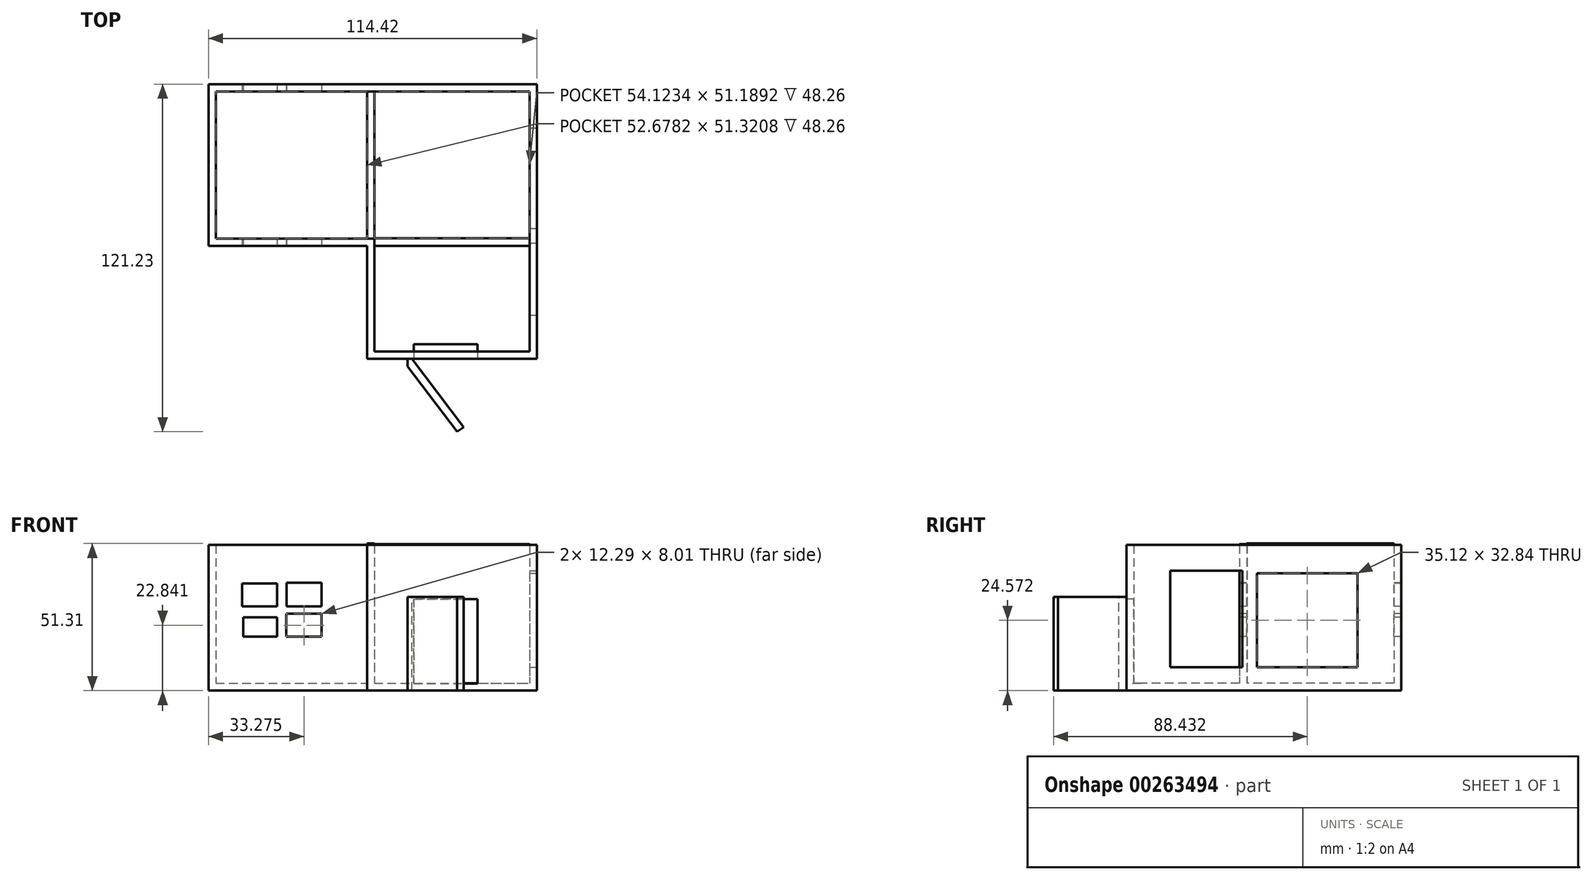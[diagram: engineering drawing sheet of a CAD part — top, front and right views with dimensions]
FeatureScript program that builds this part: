
annotation { "Feature Type Name" : "Feature", "Feature Type Description" : "" }
export const myFeature = defineFeature(function(context is Context, id is Id, definition is map)
    precondition{}
    {
        {
            var Q0;
            Q0=qCreatedBy(makeId("Top.planeOp"),FACE);
            var sketch = newSketch(context, id + "F0", { "sketchPlane" : qUnion([Q0])});
            skLineSegment(sketch, "E0.bottom", {"start": v(-55.22, 56.4) * mm, "end": v(59.2, 56.4) * mm});
            skLineSegment(sketch, "E0.top", {"start": v(-55.22, 0) * mm, "end": v(59.2, 0) * mm});
            skLineSegment(sketch, "E0.left", {"start": v(-55.22, 56.4) * mm, "end": v(-55.22, 0) * mm});
            skLineSegment(sketch, "E0.right", {"start": v(59.2, 56.4) * mm, "end": v(59.2, 0) * mm});
            skLineSegment(sketch, "E1.bottom", {"start": v(0, 0) * mm, "end": v(59.2, 0) * mm});
            skLineSegment(sketch, "E1.top", {"start": v(0, -39.43) * mm, "end": v(59.2, -39.43) * mm});
            skLineSegment(sketch, "E1.left", {"start": v(0, 0) * mm, "end": v(0, -39.43) * mm});
            skLineSegment(sketch, "E1.right", {"start": v(59.2, 0) * mm, "end": v(59.2, -39.43) * mm});
            skSolve(sketch);
        }
        {
            var Q0;
            Q0 = qSketchRegion(id + "F0", true);
            extrude(context, id + "F1", {"entities" : qUnion([Q0]), "depth" : 50.8 * mm});
        }
        {
            var Q0;
            Q0=makeQuery(id+"F1.opExtrude","CAP_FACE",FACE,{"disambiguationData":[OSD([sQuery(id+"F0.wireOp",EDGE,"E0.bottom"),sQuery(id+"F0.wireOp",EDGE,"E0.top"),sQuery(id+"F0.wireOp",EDGE,"E0.left"),sQuery(id+"F0.wireOp",EDGE,"E0.right"),sQuery(id+"F0.wireOp",EDGE,"E1.top"),sQuery(id+"F0.wireOp",EDGE,"E1.left"),sQuery(id+"F0.wireOp",EDGE,"E1.right")])],"isStart":false});
            shell(context, id + "F2", {"entities" : qUnion([Q0]), "thickness" : 2.54 * mm});
        }
        {
            var Q0;
            Q0=qCreatedBy(makeId("Front.planeOp"),FACE);
            var sketch = newSketch(context, id + "F3", { "sketchPlane" : qUnion([Q0])});
            skLineSegment(sketch, "E2.bottom", {"start": v(-43.44, 37.36) * mm, "end": v(-31.3, 37.36) * mm});
            skLineSegment(sketch, "E2.top", {"start": v(-43.44, 29.33) * mm, "end": v(-31.3, 29.33) * mm});
            skLineSegment(sketch, "E2.left", {"start": v(-43.44, 37.36) * mm, "end": v(-43.44, 29.33) * mm});
            skLineSegment(sketch, "E2.right", {"start": v(-31.3, 37.36) * mm, "end": v(-31.3, 29.33) * mm});
            skLineSegment(sketch, "E3.bottom", {"start": v(-27.97, 37.58) * mm, "end": v(-15.8, 37.58) * mm});
            skLineSegment(sketch, "E3.top", {"start": v(-27.97, 29.33) * mm, "end": v(-15.8, 29.33) * mm});
            skLineSegment(sketch, "E3.left", {"start": v(-27.97, 37.58) * mm, "end": v(-27.97, 29.33) * mm});
            skLineSegment(sketch, "E3.right", {"start": v(-15.8, 37.58) * mm, "end": v(-15.8, 29.33) * mm});
            skLineSegment(sketch, "E4.bottom", {"start": v(-28.1, 26.85) * mm, "end": v(-15.8, 26.85) * mm});
            skLineSegment(sketch, "E4.top", {"start": v(-28.1, 18.83) * mm, "end": v(-15.8, 18.83) * mm});
            skLineSegment(sketch, "E4.left", {"start": v(-28.1, 26.85) * mm, "end": v(-28.1, 18.83) * mm});
            skLineSegment(sketch, "E4.right", {"start": v(-15.8, 26.85) * mm, "end": v(-15.8, 18.83) * mm});
            skLineSegment(sketch, "E5.bottom", {"start": v(-31.3, 25.54) * mm, "end": v(-43.11, 25.54) * mm});
            skLineSegment(sketch, "E5.top", {"start": v(-31.3, 18.83) * mm, "end": v(-43.11, 18.83) * mm});
            skLineSegment(sketch, "E5.left", {"start": v(-31.3, 25.54) * mm, "end": v(-31.3, 18.83) * mm});
            skLineSegment(sketch, "E5.right", {"start": v(-43.11, 25.54) * mm, "end": v(-43.11, 18.83) * mm});
            skSolve(sketch);
        }
        {
            var Q0;
            Q0 = qSketchRegion(id + "F3", true);
            extrude(context, id + "F4", {"entities" : qUnion([Q0]), "operationType" : NewBodyOperationType.REMOVE, "oppositeDirection" : true, "depth" : 304.8 * mm});
        }
        {
            var Q0;
            Q0=makeQuery(id+"F1.opExtrude","SWEPT_FACE",FACE,{"disambiguationData":[OSD([sQuery(id+"F0.wireOp",EDGE,"E0.right"),sQuery(id+"F0.wireOp",EDGE,"E1.right")])]});
            var sketch = newSketch(context, id + "F5", { "sketchPlane" : qUnion([Q0])});
            skLineSegment(sketch, "E6.bottom", {"start": v(-24.19, 41.82) * mm, "end": v(0.96, 41.82) * mm});
            skLineSegment(sketch, "E6.top", {"start": v(-24.19, 8.15) * mm, "end": v(0.96, 8.15) * mm});
            skLineSegment(sketch, "E6.left", {"start": v(-24.19, 41.82) * mm, "end": v(-24.19, 8.15) * mm});
            skLineSegment(sketch, "E6.right", {"start": v(0.96, 41.82) * mm, "end": v(0.96, 8.15) * mm});
            skLineSegment(sketch, "E7.bottom", {"start": v(6.04, 41) * mm, "end": v(41.16, 41) * mm});
            skLineSegment(sketch, "E7.top", {"start": v(6.04, 8.15) * mm, "end": v(41.16, 8.15) * mm});
            skLineSegment(sketch, "E7.left", {"start": v(6.04, 41) * mm, "end": v(6.04, 8.15) * mm});
            skLineSegment(sketch, "E7.right", {"start": v(41.16, 41) * mm, "end": v(41.16, 8.15) * mm});
            skSolve(sketch);
        }
        {
            var Q0;
            Q0=makeQuery(id+"F5.imprint","IMPRINT",FACE,{"disambiguationData":[TD([[makeQuery(id+"F5.imprint","IMPRINT",EDGE,{"derivedFrom":sQuery(id+"F5.wireOp",EDGE,"E6.bottom")}),-1.0]])]});
            var Q1;
            Q1=makeQuery(id+"F5.imprint","IMPRINT",FACE,{"disambiguationData":[TD([[makeQuery(id+"F5.imprint","IMPRINT",EDGE,{"derivedFrom":sQuery(id+"F5.wireOp",EDGE,"E7.bottom")}),-1.0]])]});
            extrude(context, id + "F6", {"entities" : qUnion([Q0, Q1]), "operationType" : NewBodyOperationType.REMOVE, "oppositeDirection" : true, "depth" : 25.4 * mm});
        }
        {
            var Q0;
            Q0=makeQuery(id+"F1.opExtrude","SWEPT_FACE",FACE,{"disambiguationData":[OSD([sQuery(id+"F0.wireOp",EDGE,"E1.top")])]});
            var sketch = newSketch(context, id + "F7", { "sketchPlane" : qUnion([Q0])});
            skLineSegment(sketch, "E8.bottom", {"start": v(14.19, 0) * mm, "end": v(33.68, 0) * mm});
            skLineSegment(sketch, "E8.top", {"start": v(14.19, 32.67) * mm, "end": v(33.68, 32.67) * mm});
            skLineSegment(sketch, "E8.left", {"start": v(14.19, 0) * mm, "end": v(14.19, 32.67) * mm});
            skLineSegment(sketch, "E8.right", {"start": v(33.68, 0) * mm, "end": v(33.68, 32.67) * mm});
            skSolve(sketch);
        }
        {
            var Q0;
            Q0 = qSketchRegion(id + "F7", true);
            extrude(context, id + "F8", {"entities" : qUnion([Q0]), "operationType" : NewBodyOperationType.ADD, "depth" : 25.4 * mm});
        }
        {
            var Q0;
            Q0=makeQuery(id+"F8.opExtrude","SWEPT_FACE",FACE,{"disambiguationData":[OSD([sQuery(id+"F7.wireOp",EDGE,"E8.top")])]});
            var sketch = newSketch(context, id + "F9", { "sketchPlane" : qUnion([Q0])});
            skLineSegment(sketch, "E9", {"start": v(14.19, -64.83) * mm, "end": v(31.46, -64.83) * mm});
            skLineSegment(sketch, "E10", {"start": v(31.46, -64.83) * mm, "end": v(14.19, -42.1) * mm});
            skLineSegment(sketch, "E11", {"start": v(14.19, -42.1) * mm, "end": v(14.19, -64.83) * mm});
            skSolve(sketch);
        }
        {
            var Q0;
            Q0 = qSketchRegion(id + "F9", true);
            extrude(context, id + "F10", {"entities" : qUnion([Q0]), "operationType" : NewBodyOperationType.REMOVE, "oppositeDirection" : true, "depth" : 44.96 * mm});
        }
        {
            var Q0;
            Q0=makeQuery(id+"F8.opExtrude","SWEPT_FACE",FACE,{"disambiguationData":[OSD([sQuery(id+"F7.wireOp",EDGE,"E8.top")])]});
            var sketch = newSketch(context, id + "F11", { "sketchPlane" : qUnion([Q0])});
            skLineSegment(sketch, "E12", {"start": v(33.68, -63.3) * mm, "end": v(33.68, -39.43) * mm});
            skLineSegment(sketch, "E13", {"start": v(33.68, -39.43) * mm, "end": v(15.74, -39.43) * mm});
            skLineSegment(sketch, "E14", {"start": v(15.74, -39.43) * mm, "end": v(33.68, -63.3) * mm});
            skSolve(sketch);
        }
        {
            var Q0;
            Q0=makeQuery(id+"F11.imprint","IMPRINT",FACE,{"disambiguationData":[TD([[makeQuery(id+"F11.imprint","IMPRINT",EDGE,{"derivedFrom":sQuery(id+"F11.wireOp",EDGE,"E12")}),1.0]])]});
            extrude(context, id + "F12", {"entities" : qUnion([Q0]), "operationType" : NewBodyOperationType.REMOVE, "oppositeDirection" : true, "depth" : 45.97 * mm});
        }
        {
            var Q0;
            Q0=makeQuery(id+"F8.opExtrude","SWEPT_FACE",FACE,{"disambiguationData":[OSD([sQuery(id+"F7.wireOp",EDGE,"E8.top")])]});
            var sketch = newSketch(context, id + "F13", { "sketchPlane" : qUnion([Q0])});
            skLineSegment(sketch, "E15", {"start": v(31.46, -64.83) * mm, "end": v(33.68, -63.3) * mm});
            skLineSegment(sketch, "E16", {"start": v(33.68, -63.3) * mm, "end": v(33.68, -64.83) * mm});
            skLineSegment(sketch, "E17", {"start": v(33.68, -64.83) * mm, "end": v(31.46, -64.83) * mm});
            skSolve(sketch);
        }
        {
            var Q0;
            Q0 = qSketchRegion(id + "F13", true);
            extrude(context, id + "F14", {"entities" : qUnion([Q0]), "operationType" : NewBodyOperationType.REMOVE, "oppositeDirection" : true, "depth" : 38.1 * mm});
        }
        {
            var Q0;
            Q0=makeQuery(id+"F12.boolean.opBoolean","MERGE",FACE,{"derivedFrom":[makeQuery(id+"F1.opExtrude","SWEPT_FACE",FACE,{"disambiguationData":[OSD([sQuery(id+"F0.wireOp",EDGE,"E1.top")])]}),makeQuery(id+"F12.opExtrude","SWEPT_FACE",FACE,{"disambiguationData":[OSD([sQuery(id+"F11.wireOp",EDGE,"E13")])]})]});
            var sketch = newSketch(context, id + "F15", { "sketchPlane" : qUnion([Q0])});
            skLineSegment(sketch, "E18.bottom", {"start": v(15.74, 32.67) * mm, "end": v(40.13, 32.67) * mm});
            skLineSegment(sketch, "E18.top", {"start": v(15.74, 0) * mm, "end": v(40.13, 0) * mm});
            skLineSegment(sketch, "E18.left", {"start": v(15.74, 32.67) * mm, "end": v(15.74, 0) * mm});
            skLineSegment(sketch, "E18.right", {"start": v(40.13, 32.67) * mm, "end": v(40.13, 0) * mm});
            skSolve(sketch);
        }
        {
            var Q0;
            Q0=makeQuery(id+"F15.imprint","IMPRINT",FACE,{"disambiguationData":[TD([[makeQuery(id+"F15.imprint","IMPRINT",EDGE,{"derivedFrom":sQuery(id+"F15.wireOp",EDGE,"E18.bottom")}),-1.0]])]});
            var sketch = newSketch(context, id + "F16", { "sketchPlane" : qUnion([Q0])});
            skLineSegment(sketch, "E19.bottom", {"start": v(16.34, 31.96) * mm, "end": v(38.5, 31.96) * mm});
            skLineSegment(sketch, "E19.top", {"start": v(16.34, 2.42) * mm, "end": v(38.5, 2.42) * mm});
            skLineSegment(sketch, "E19.left", {"start": v(16.34, 31.96) * mm, "end": v(16.34, 2.42) * mm});
            skLineSegment(sketch, "E19.right", {"start": v(38.5, 31.96) * mm, "end": v(38.5, 2.42) * mm});
            skSolve(sketch);
        }
        {
            var Q0;
            Q0 = qSketchRegion(id + "F16", true);
            extrude(context, id + "F17", {"entities" : qUnion([Q0]), "operationType" : NewBodyOperationType.REMOVE, "oppositeDirection" : true, "depth" : 5.08 * mm});
        }
        {
            var Q0;
            Q0=makeQuery(id+"F2.opShell","OFFSET_FACE",FACE,{"disambiguationData":[OSD([sQuery(id+"F0.wireOp",EDGE,"E0.bottom"),sQuery(id+"F0.wireOp",EDGE,"E0.top"),sQuery(id+"F0.wireOp",EDGE,"E0.left"),sQuery(id+"F0.wireOp",EDGE,"E0.right"),sQuery(id+"F0.wireOp",EDGE,"E1.top"),sQuery(id+"F0.wireOp",EDGE,"E1.left"),sQuery(id+"F0.wireOp",EDGE,"E1.right")])]});
            var sketch = newSketch(context, id + "F18", { "sketchPlane" : qUnion([Q0])});
            skLineSegment(sketch, "E20", {"start": v(2.54, 2.54) * mm, "end": v(2.54, 53.86) * mm});
            skLineSegment(sketch, "E21", {"start": v(2.54, 53.86) * mm, "end": v(0, 53.86) * mm});
            skLineSegment(sketch, "E22", {"start": v(0, 53.86) * mm, "end": v(0, 2.54) * mm});
            skLineSegment(sketch, "E23", {"start": v(0, 2.54) * mm, "end": v(2.54, 2.54) * mm});
            skLineSegment(sketch, "E24", {"start": v(2.54, 2.54) * mm, "end": v(56.66, 2.54) * mm});
            skLineSegment(sketch, "E25", {"start": v(56.66, 2.54) * mm, "end": v(56.66, 0) * mm});
            skLineSegment(sketch, "E26", {"start": v(56.66, 0) * mm, "end": v(2.54, 0) * mm});
            skLineSegment(sketch, "E27", {"start": v(2.54, 0) * mm, "end": v(2.54, 2.54) * mm});
            skSolve(sketch);
        }
        {
            var Q0;
            Q0=makeQuery(id+"F18.imprint","IMPRINT",FACE,{"disambiguationData":[TD([[makeQuery(id+"F18.imprint","IMPRINT",EDGE,{"derivedFrom":sQuery(id+"F18.wireOp",EDGE,"E20")}),1.0]])]});
            extrude(context, id + "F19", {"entities" : qUnion([Q0]), "operationType" : NewBodyOperationType.ADD, "depth" : 48.77 * mm});
        }
        {
            var Q0;
            {var subQ0=sQuery(id+"F0.wireOp",EDGE,"E1.left");var subQ1=sQuery(id+"F0.wireOp",EDGE,"E1.top");var subQ2=sQuery(id+"F0.wireOp",EDGE,"E1.right");var subQ3=sQuery(id+"F0.wireOp",EDGE,"E0.right");var subQ5=sQuery(id+"F0.wireOp",EDGE,"E0.bottom");Q0=makeQuery(id+"F19.boolean.opBoolean","SPLIT",FACE,{"disambiguationData":[TD([makeQuery(id+"F2.opShell","OFFSET_FACE",FACE,{"disambiguationData":[OSD([subQ1])]})])],"derivedFrom":makeQuery(id+"F2.opShell","OFFSET_FACE",FACE,{"disambiguationData":[OSD([subQ5,sQuery(id+"F0.wireOp",EDGE,"E0.top"),sQuery(id+"F0.wireOp",EDGE,"E0.left"),subQ3,subQ1,subQ0,subQ2])]})});}
            var sketch = newSketch(context, id + "F20", { "sketchPlane" : qUnion([Q0])});
            skLineSegment(sketch, "E28", {"start": v(56.66, 0) * mm, "end": v(56.66, 2.67) * mm});
            skLineSegment(sketch, "E29", {"start": v(56.66, 2.67) * mm, "end": v(2.54, 2.67) * mm});
            skLineSegment(sketch, "E30", {"start": v(2.54, 2.67) * mm, "end": v(2.54, 0) * mm});
            skLineSegment(sketch, "E31", {"start": v(2.54, 0) * mm, "end": v(56.66, 0) * mm});
            skSolve(sketch);
        }
        {
            var Q0;
            Q0 = qSketchRegion(id + "F20", true);
            extrude(context, id + "F21", {"entities" : qUnion([Q0]), "operationType" : NewBodyOperationType.ADD, "depth" : 48.5 * mm});
        }
    });
